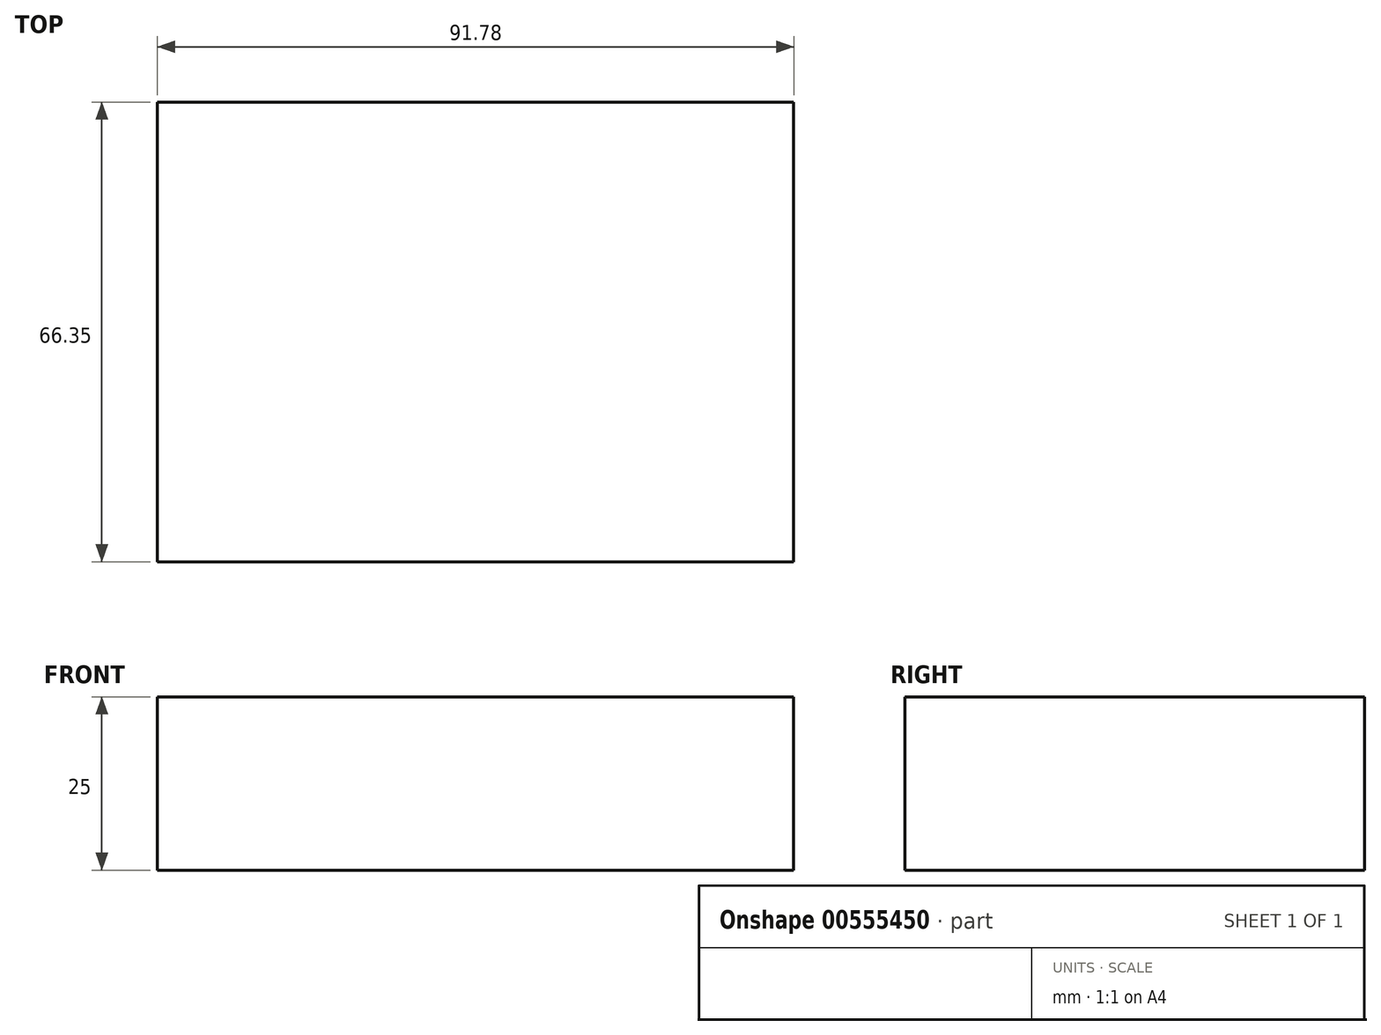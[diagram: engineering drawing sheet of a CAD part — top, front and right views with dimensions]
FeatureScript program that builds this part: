
annotation { "Feature Type Name" : "Feature", "Feature Type Description" : "" }
export const myFeature = defineFeature(function(context is Context, id is Id, definition is map)
    precondition{}
    {
        {
            var Q0;
            Q0=qCreatedBy(makeId("Top.planeOp"),FACE);
            var sketch = newSketch(context, id + "F0", { "sketchPlane" : qUnion([Q0])});
            skLineSegment(sketch, "E0.bottom", {"start": v(-42.1, 42.17) * mm, "end": v(49.68, 42.17) * mm});
            skLineSegment(sketch, "E0.top", {"start": v(-42.1, -24.18) * mm, "end": v(49.68, -24.18) * mm});
            skLineSegment(sketch, "E0.left", {"start": v(-42.1, 42.17) * mm, "end": v(-42.1, -24.18) * mm});
            skLineSegment(sketch, "E0.right", {"start": v(49.68, 42.17) * mm, "end": v(49.68, -24.18) * mm});
            skSolve(sketch);
        }
        {
            var Q0;
            Q0=makeQuery(id+"F0.imprint","IMPRINT",FACE,{"disambiguationData":[TD([[makeQuery(id+"F0.imprint","IMPRINT",EDGE,{"derivedFrom":sQuery(id+"F0.wireOp",EDGE,"E0.bottom")}),-1.0]])]});
            var sketch = newSketch(context, id + "F1", { "sketchPlane" : qUnion([Q0])});
            skSolve(sketch);
        }
        {
            var Q0;
            Q0 = qSketchRegion(id + "F1", true);
            var Q1;
            Q1=makeQuery(id+"F0.imprint","IMPRINT",FACE,{"disambiguationData":[TD([[makeQuery(id+"F0.imprint","IMPRINT",EDGE,{"derivedFrom":sQuery(id+"F0.wireOp",EDGE,"E0.bottom")}),-1.0]])]});
            extrude(context, id + "F2", {"entities" : qUnion([Q0, Q1]), "depth" : 25 * mm, "offsetDistance" : 25 * mm});
        }
    });
